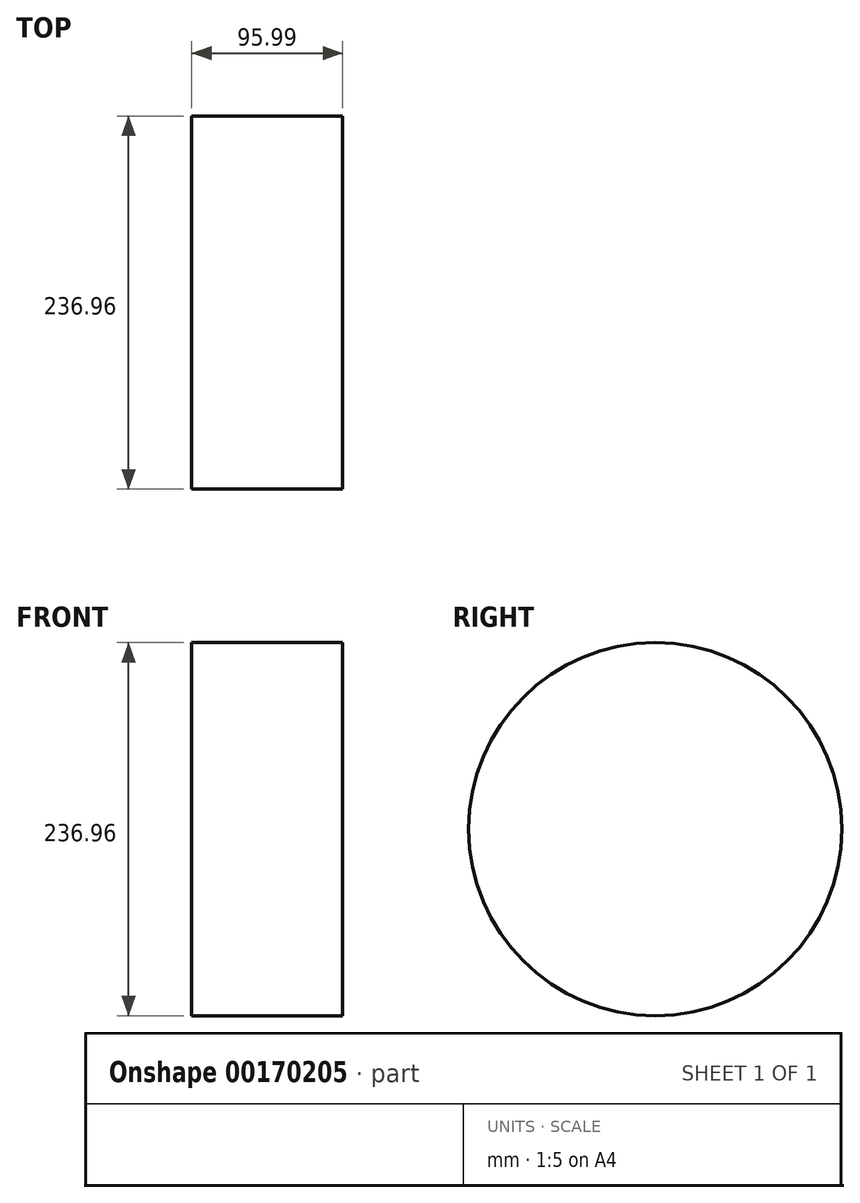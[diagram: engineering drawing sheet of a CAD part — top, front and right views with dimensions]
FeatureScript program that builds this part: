
annotation { "Feature Type Name" : "Feature", "Feature Type Description" : "" }
export const myFeature = defineFeature(function(context is Context, id is Id, definition is map)
    precondition{}
    {
        {
            var Q0;
            Q0=qCreatedBy(makeId("Right.planeOp"),FACE);
            var sketch = newSketch(context, id + "F0", { "sketchPlane" : qUnion([Q0])});
            skCircle(sketch, "E0", {"center": v(0, 0) * mm, "radius": 118.48 * mm});
            skSolve(sketch);
        }
        {
            var Q0;
            Q0=makeQuery(id+"F0.imprint","IMPRINT",FACE,{"disambiguationData":[TD([[makeQuery(id+"F0.imprint","IMPRINT",EDGE,{"derivedFrom":sQuery(id+"F0.wireOp",EDGE,"E0")}),1.0]])]});
            extrude(context, id + "F1", {"entities" : qUnion([Q0]), "depth" : 95.99 * mm});
        }
    });
